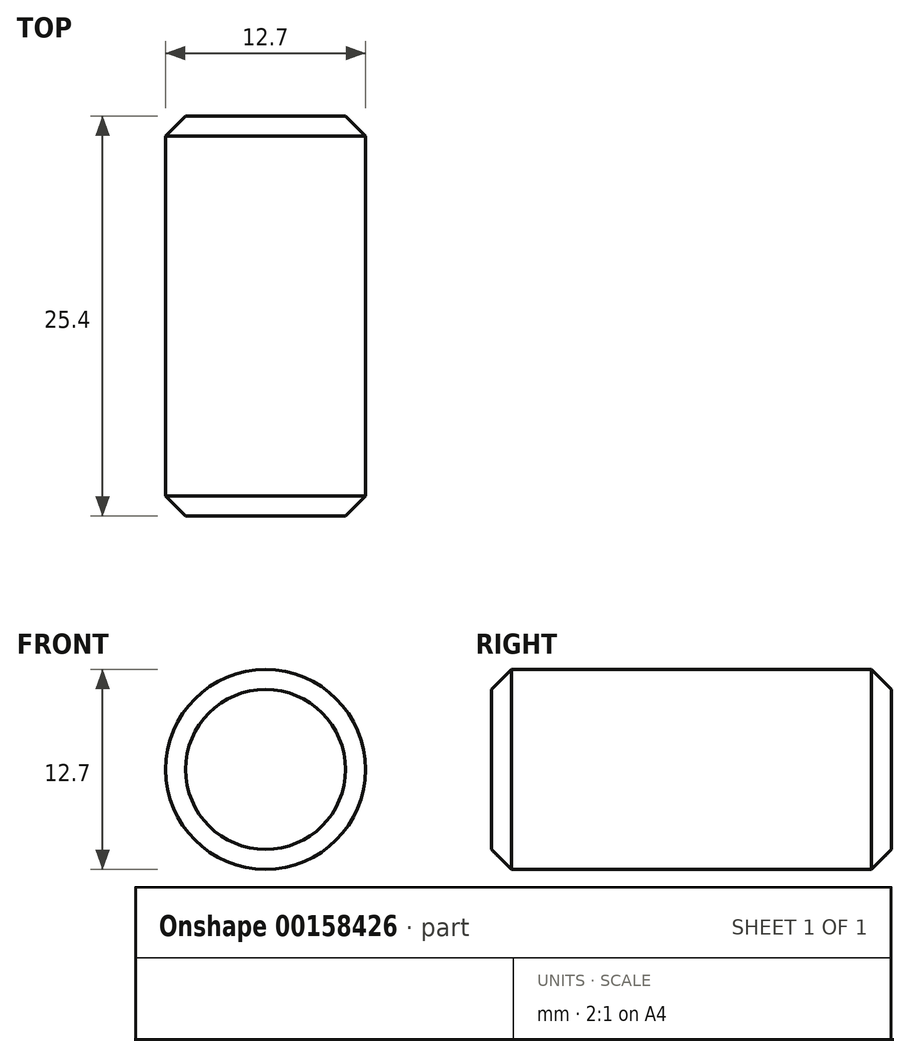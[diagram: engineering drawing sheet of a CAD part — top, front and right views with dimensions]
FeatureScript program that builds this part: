
annotation { "Feature Type Name" : "Feature", "Feature Type Description" : "" }
export const myFeature = defineFeature(function(context is Context, id is Id, definition is map)
    precondition{}
    {
        {
            var Q0;
            Q0=qCreatedBy(makeId("Front.planeOp"),FACE);
            var sketch = newSketch(context, id + "F0", { "sketchPlane" : qUnion([Q0])});
            skCircle(sketch, "E0", {"center": v(0, 0) * mm, "radius": 6.35 * mm});
            skSolve(sketch);
        }
        {
            var Q0;
            Q0=makeQuery(id+"F0.imprint","IMPRINT",FACE,{"disambiguationData":[TD([[makeQuery(id+"F0.imprint","IMPRINT",EDGE,{"derivedFrom":sQuery(id+"F0.wireOp",EDGE,"E0")}),1.0]])]});
            extrude(context, id + "F1", {"entities" : qUnion([Q0]), "depth" : 25.4 * mm});
        }
        {
            var Q0;
            Q0=makeQuery(id+"F1.opExtrude","CAP_EDGE",EDGE,{"disambiguationData":[OSD([sQuery(id+"F0.wireOp",EDGE,"E0")])],"isStart":false});
            chamfer(context, id + "F2", {"entities" : qUnion([Q0]), "width" : 1.27 * mm, "tangentPropagation" : true});
        }
        {
            var Q0;
            Q0=makeQuery(id+"F1.opExtrude","CAP_EDGE",EDGE,{"disambiguationData":[OSD([sQuery(id+"F0.wireOp",EDGE,"E0")])],"isStart":true});
            chamfer(context, id + "F3", {"entities" : qUnion([Q0]), "width" : 1.27 * mm, "tangentPropagation" : true});
        }
    });
